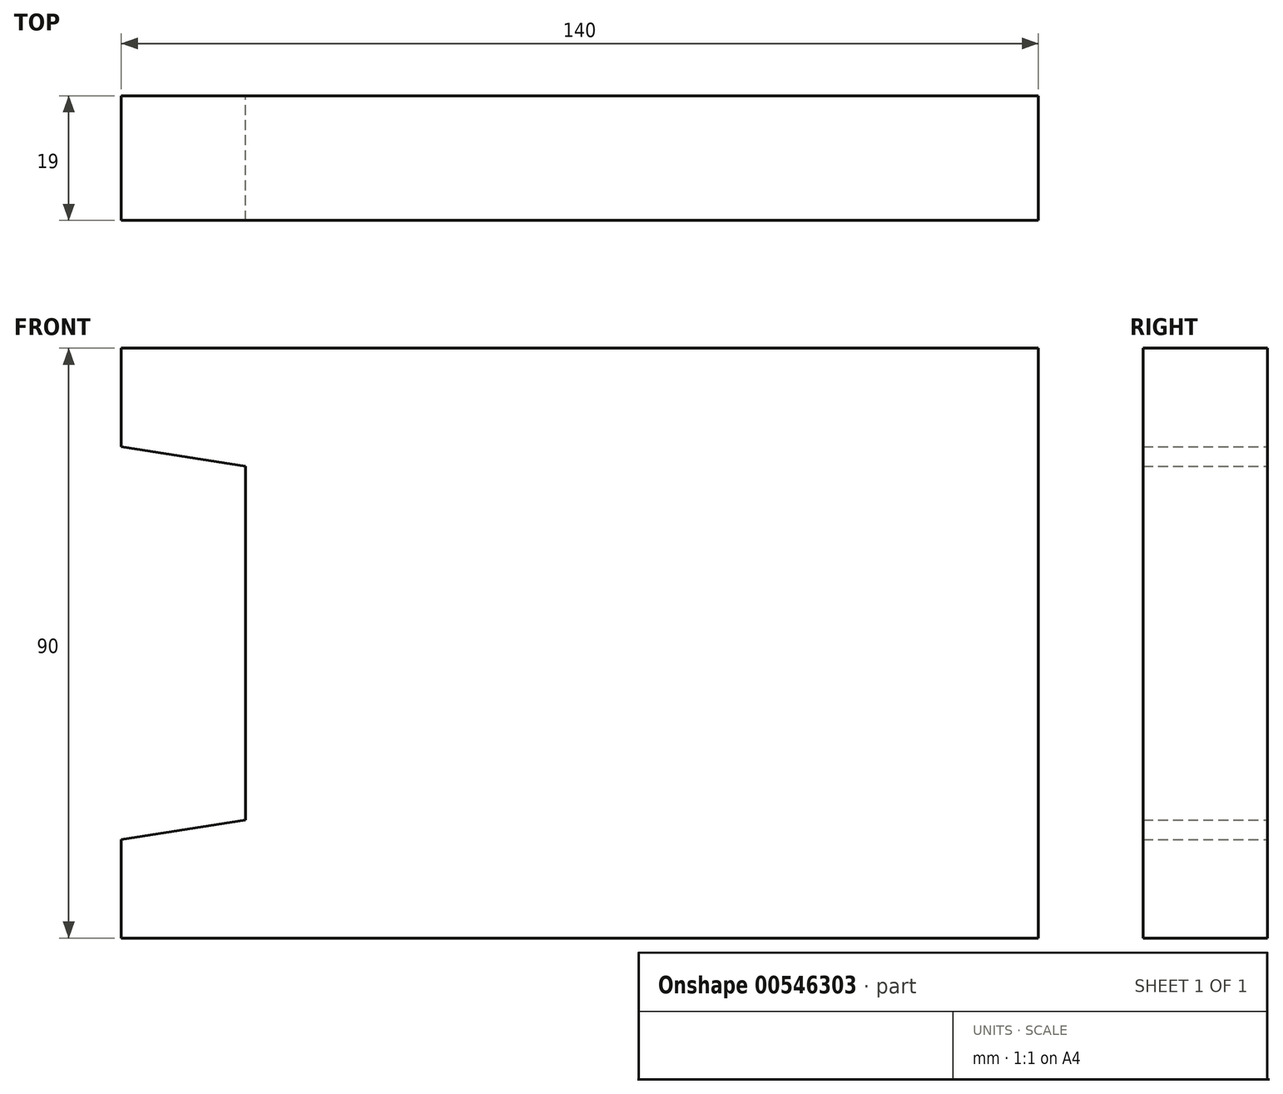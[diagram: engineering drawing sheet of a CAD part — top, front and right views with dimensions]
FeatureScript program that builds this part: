
annotation { "Feature Type Name" : "Feature", "Feature Type Description" : "" }
export const myFeature = defineFeature(function(context is Context, id is Id, definition is map)
    precondition{}
    {
        {
            var Q0;
            Q0=qCreatedBy(makeId("Front.planeOp"),FACE);
            var sketch = newSketch(context, id + "F0", { "sketchPlane" : qUnion([Q0])});
            skLineSegment(sketch, "E0.bottom", {"start": v(-70, 45) * mm, "end": v(70, 45) * mm});
            skLineSegment(sketch, "E0.top", {"start": v(-70, -45) * mm, "end": v(70, -45) * mm});
            skLineSegment(sketch, "E0.left", {"start": v(-70, 45) * mm, "end": v(-70, 30) * mm});
            skLineSegment(sketch, "E0.right", {"start": v(70, 45) * mm, "end": v(70, -45) * mm});
            skPoint(sketch, "E0.middle", {"position": v(0, 0) * mm});
            skLineSegment(sketch, "E1", {"start": v(-51, 27) * mm, "end": v(-51, -27) * mm});
            skLineSegment(sketch, "E2", {"start": v(-70, 30) * mm, "end": v(-51, 27) * mm});
            skLineSegment(sketch, "E3.trimOffspring", {"start": v(-70, -30) * mm, "end": v(-70, -45) * mm});
            skLineSegment(sketch, "E4.MirrorCS", {"start": v(-70, -30) * mm, "end": v(-51, -27) * mm});
            skSolve(sketch);
        }
        {
            var Q0;
            Q0=makeQuery(id+"F0.imprint","IMPRINT",FACE,{"disambiguationData":[TD([[makeQuery(id+"F0.imprint","IMPRINT",EDGE,{"derivedFrom":sQuery(id+"F0.wireOp",EDGE,"E0.bottom")}),-1.0]])]});
            extrude(context, id + "F1", {"entities" : qUnion([Q0]), "depth" : 19 * mm, "offsetDistance" : 25 * mm});
        }
    });
